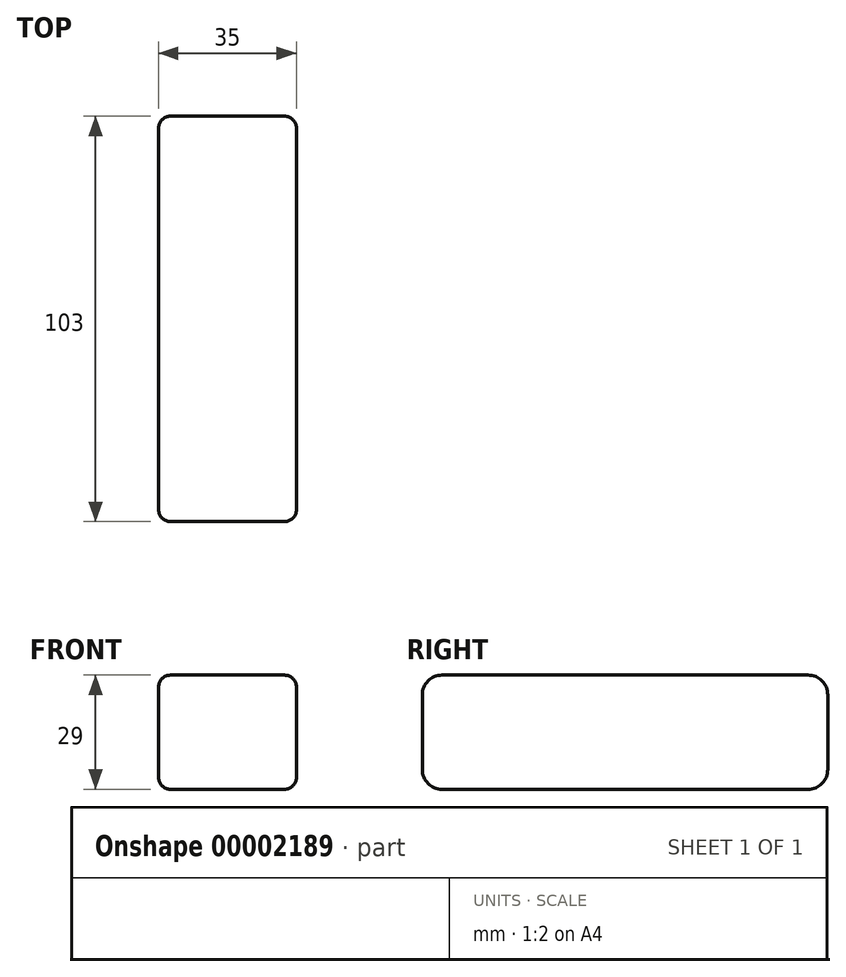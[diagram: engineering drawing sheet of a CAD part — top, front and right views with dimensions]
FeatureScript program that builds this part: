
annotation { "Feature Type Name" : "Feature", "Feature Type Description" : "" }
export const myFeature = defineFeature(function(context is Context, id is Id, definition is map)
    precondition{}
    {
        {
            var Q0;
            Q0=qCreatedBy(makeId("Top.planeOp"),FACE);
            var sketch = newSketch(context, id + "F0", { "sketchPlane" : qUnion([Q0])});
            skLineSegment(sketch, "E0.rect.bottom", {"start": v(17.5, -51.5) * mm, "end": v(-17.5, -51.5) * mm});
            skLineSegment(sketch, "E0.rect.top", {"start": v(17.5, 51.5) * mm, "end": v(-17.5, 51.5) * mm});
            skLineSegment(sketch, "E0.rect.left", {"start": v(17.5, -51.5) * mm, "end": v(17.5, 51.5) * mm});
            skLineSegment(sketch, "E0.rect.right", {"start": v(-17.5, -51.5) * mm, "end": v(-17.5, 51.5) * mm});
            skPoint(sketch, "E0.rect.middle", {"position": v(0, 0) * mm});
            skSolve(sketch);
        }
        {
            var Q0;
            Q0 = qSketchRegion(id + "F0", true);
            extrude(context, id + "F1", {"entities" : qUnion([Q0]), "depth" : 29 * mm});
        }
        {
            var Q0;
            Q0=makeQuery(id+"F1.opExtrude","CAP_EDGE",EDGE,{"disambiguationData":[OSD([sQuery(id+"F0.wireOp",EDGE,"E0.rect.bottom")])],"isStart":false});
            var Q1;
            Q1=makeQuery(id+"F1.opExtrude","CAP_EDGE",EDGE,{"disambiguationData":[OSD([sQuery(id+"F0.wireOp",EDGE,"E0.rect.bottom")])],"isStart":true});
            var Q2;
            Q2=makeQuery(id+"F1.opExtrude","CAP_EDGE",EDGE,{"disambiguationData":[OSD([sQuery(id+"F0.wireOp",EDGE,"E0.rect.top")])],"isStart":false});
            var Q3;
            Q3=makeQuery(id+"F1.opExtrude","CAP_EDGE",EDGE,{"disambiguationData":[OSD([sQuery(id+"F0.wireOp",EDGE,"E0.rect.top")])],"isStart":true});
            fillet(context, id + "F2", {"entities" : qUnion([Q0, Q1, Q2, Q3]), "radius" : 5 * mm, "tangentPropagation" : true, "allowEdgeOverflow" : false});
        }
        {
            var Q0;
            Q0=makeQuery(id+"F1.opExtrude","CAP_EDGE",EDGE,{"disambiguationData":[OSD([sQuery(id+"F0.wireOp",EDGE,"E0.rect.left")])],"isStart":false});
            var Q1;
            Q1=makeQuery(id+"F1.opExtrude","CAP_EDGE",EDGE,{"disambiguationData":[OSD([sQuery(id+"F0.wireOp",EDGE,"E0.rect.right")])],"isStart":false});
            fillet(context, id + "F3", {"entities" : qUnion([Q0, Q1]), "radius" : 3 * mm, "tangentPropagation" : true, "allowEdgeOverflow" : false});
        }
    });
